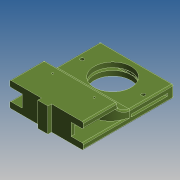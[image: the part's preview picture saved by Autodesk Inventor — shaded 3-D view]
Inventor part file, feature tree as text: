
AUTODESK INVENTOR PART (.ipt)
format: ipt  version: 2015 SP1 (Build 190203100, 203)  size: 516,096 bytes
history: native  units: mm
features: sketch x12, extrude x7, fillet x7, projected_geometry x6, hole x5, mirror x3
ambient origin geometry x8: Origin, YZ Plane, XZ Plane, XY Plane, X Axis, Y Axis, Z Axis, Center Point
bodies: Solid2 (feature_tree)
feature tree (40):
  extrude  "Extrusion2"  Depth=3.0mm
  extrude  "Extrusion3"  Depth=5.0mm
  hole  "Trou pour ressort"  [1 undecoded]
  mirror  "Mirror1"
  extrude  "Extrusion4"  Depth=30.0mm
  extrude  "Extrusion5"  Depth=20.0mm
  extrude  "Extrusion6"  Depth=25.0mm
  hole  "Hole4"  [1 undecoded]
  fillet  "Fillet3"  Radius=3.0mm
  hole  "Hole5"  [1 undecoded]
  extrude  "Extrusion13"  Depth=11.5mm
  fillet  "Fillet25"  Radius=10.0mm
  fillet  "Fillet26"  Radius=10.0mm
  fillet  "Fillet27"  Radius=10.0mm
  fillet  "Fillet28"  Radius=1.0mm
  fillet  "Fillet29"  Radius=1.0mm
  extrude  "Extrusion16"  Depth=1.5mm
  fillet  "Fillet30"  Radius=1.0mm
  hole  "Hole12"  [1 undecoded]
  mirror  "Mirror4"
  hole  "Hole13"  [1 undecoded]
  mirror  "Mirror5"
  sketch  "Sketch1"  dims[d14=20.0mm d15=20.0mm d16=0.0mm d18=3.0mm]
  sketch  "Sketch3"  dims[d19=3.0mm d20=5.0mm]
  sketch  "Sketch6"  dims[d21=10.0mm d22=0.0mm d42=22.0mm]
  sketch  "Sketch7"  dims[d43=4.1mm d44=30.0mm]
  sketch  "Sketch8"  dims[d45=3.0mm d46=20.0mm]
  sketch  "Sketch9"  dims[d49=4.0mm]
  sketch  "Sketch10"  dims[d50=5.0mm d51=6.0mm d52=4.0mm d53=2.0mm d54=90.0deg d55=8.0mm d56=20.594885mm d57=25.0mm]
  sketch  "Sketch12"  dims[d58=10.0mm d59=0.0mm d60=2.0mm d61=0.0mm d62=3.0mm]
  sketch  "Sketch22"  dims[d66=16.0mm d67=50.0mm d68=0.0mm]
  sketch  "Sketch28"  dims[d69=20.0mm]
  sketch  "Sketch30"  dims[d70=30.0mm d71=6.0mm d72=50.0mm d73=18.0mm d74=90.0deg d75=8.0mm d76=20.594885mm d78=11.5mm]
  sketch  "Sketch31"  dims[d79=6.0mm d80=6.0mm d81=4.0mm d82=2.0mm d83=90.0deg d84=8.0mm d85=20.594885mm d146=10.0mm d147=10.0mm d148=0.0mm d202=10.0mm d203=1.0mm d204=1.0mm d205=1.0mm d206=1.0mm d207=2.0mm d208=30.0mm d209=4.0mm d210=10.0mm d211=0.0mm d212=0.5mm d213=25.0mm d214=3.0mm d215=6.0mm d216=4.0mm d217=2.0mm d218=90.0deg d219=5.0mm d220=0.0mm d221=3.0mm d222=1.5mm d223=6.0mm d224=4.0mm d225=2.0mm d226=90.0deg d227=2.0mm d228=20.594885mm]
  projected_geometry  "Projected Loop2"
  projected_geometry  "Project Cut Edges2"
  projected_geometry  "Project Cut Edges3"
  projected_geometry  "Project Cut Edges4"
  projected_geometry  "Project Cut Edges5"
  projected_geometry  "Project Cut Edges7"
note: 5 required parameter values undecoded (feature->parameter linkage not recoverable at this tier; creation-order binding heuristic only, values carry confidence <= 0.55)
